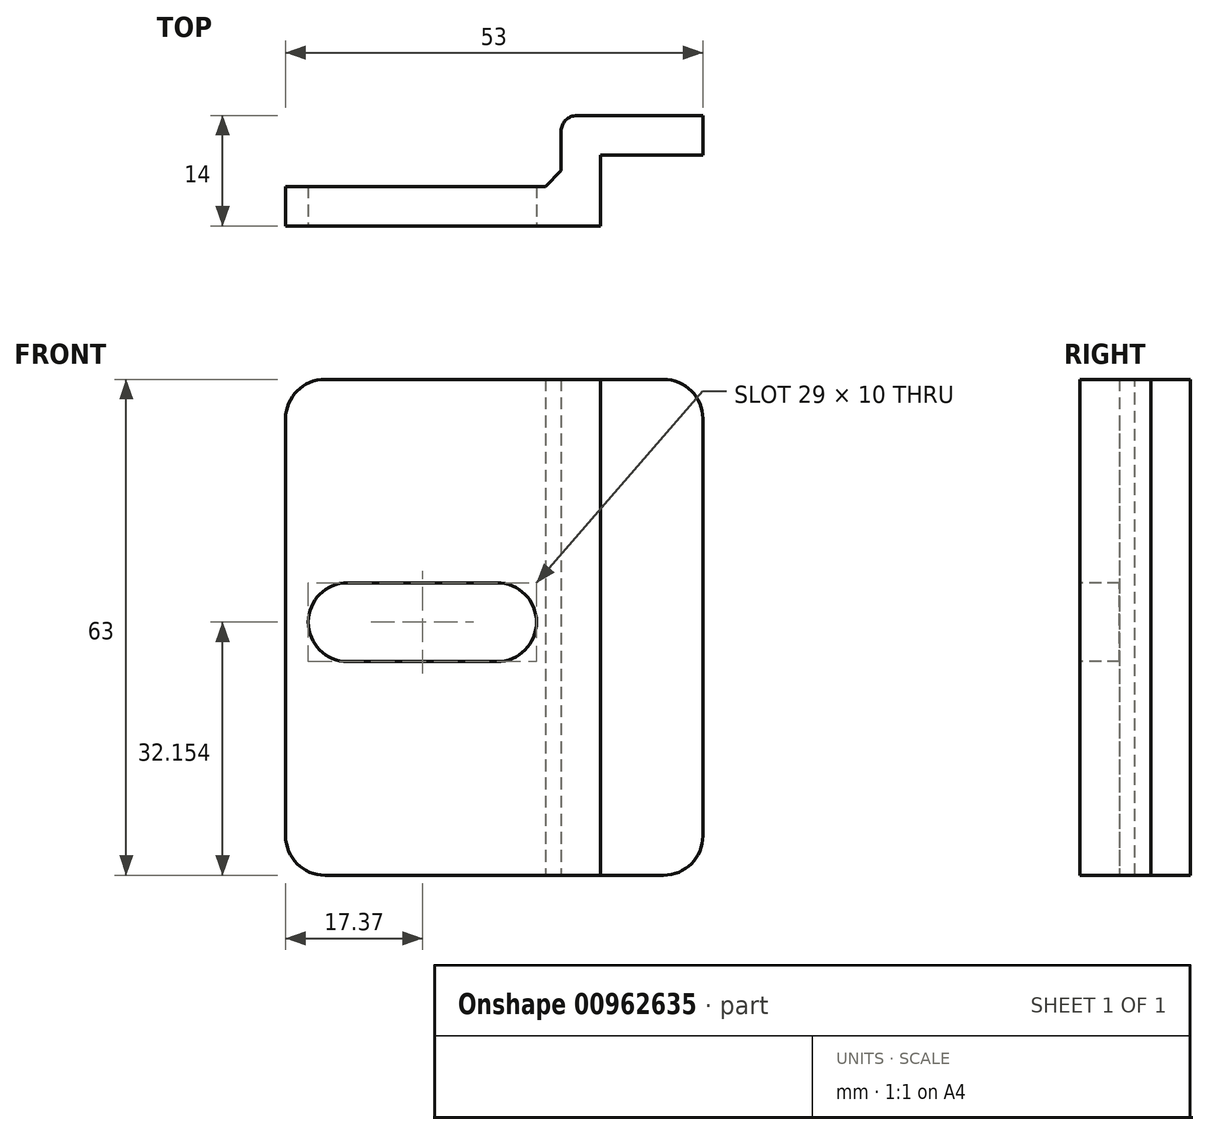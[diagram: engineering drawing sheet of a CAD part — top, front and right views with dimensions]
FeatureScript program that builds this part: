
annotation { "Feature Type Name" : "Feature", "Feature Type Description" : "" }
export const myFeature = defineFeature(function(context is Context, id is Id, definition is map)
    precondition{}
    {
        {
            var Q0;
            Q0=qCreatedBy(makeId("Top.planeOp"),FACE);
            var sketch = newSketch(context, id + "F0", { "sketchPlane" : qUnion([Q0])});
            skLineSegment(sketch, "E0.bottom", {"start": v(-6.28, 23.67) * mm, "end": v(11.72, 23.67) * mm});
            skLineSegment(sketch, "E0.top", {"start": v(-6.28, 18.67) * mm, "end": v(11.72, 18.67) * mm});
            skLineSegment(sketch, "E0.left", {"start": v(-6.28, 23.67) * mm, "end": v(-6.28, 18.67) * mm});
            skLineSegment(sketch, "E0.right", {"start": v(11.72, 23.67) * mm, "end": v(11.72, 18.67) * mm});
            skLineSegment(sketch, "E1.bottom", {"start": v(-6.28, 23.67) * mm, "end": v(-1.28, 23.67) * mm});
            skLineSegment(sketch, "E1.top", {"start": v(-6.28, 9.67) * mm, "end": v(-1.28, 9.67) * mm});
            skLineSegment(sketch, "E1.left", {"start": v(-6.28, 23.67) * mm, "end": v(-6.28, 9.67) * mm});
            skLineSegment(sketch, "E1.right", {"start": v(-1.28, 23.67) * mm, "end": v(-1.28, 9.67) * mm});
            skLineSegment(sketch, "E2.bottom", {"start": v(-6.28, 9.67) * mm, "end": v(-41.28, 9.67) * mm});
            skLineSegment(sketch, "E2.top", {"start": v(-6.28, 14.67) * mm, "end": v(-41.28, 14.67) * mm});
            skLineSegment(sketch, "E2.left", {"start": v(-6.28, 9.67) * mm, "end": v(-6.28, 14.67) * mm});
            skLineSegment(sketch, "E2.right", {"start": v(-41.28, 9.67) * mm, "end": v(-41.28, 14.67) * mm});
            skSolve(sketch);
        }
        {
            var Q0;
            {var subQ0=sQuery(id+"F0.wireOp",EDGE,"E2.bottom");Q0=makeQuery(id+"F0.imprint","IMPRINT",FACE,{"disambiguationData":[TD([[makeQuery(id+"F0.imprint","IMPRINT",EDGE,{"derivedFrom":subQ0}),-1.0]])]});}
            var Q1;
            {var subQ1=sQuery(id+"F0.wireOp",EDGE,"E1.top");Q1=makeQuery(id+"F0.imprint","IMPRINT",FACE,{"disambiguationData":[TD([[makeQuery(id+"F0.imprint","IMPRINT",EDGE,{"derivedFrom":subQ1}),1.0]])]});}
            var Q2;
            {var subQ3=sQuery(id+"F0.wireOp",EDGE,"E0.right");Q2=makeQuery(id+"F0.imprint","IMPRINT",FACE,{"disambiguationData":[TD([[makeQuery(id+"F0.imprint","IMPRINT",EDGE,{"derivedFrom":subQ3}),-1.0]])]});}
            var Q3;
            {var subQ3=sQuery(id+"F0.wireOp",EDGE,"E0.left");Q3=makeQuery(id+"F0.imprint","IMPRINT",FACE,{"disambiguationData":[TD([[makeQuery(id+"F0.imprint","IMPRINT",EDGE,{"derivedFrom":subQ3}),1.0]])]});}
            extrude(context, id + "F1", {"entities" : qUnion([Q0, Q1, Q2, Q3]), "depth" : 63 * mm, "offsetDistance" : 25 * mm});
        }
        {
            var Q0;
            Q0=makeQuery(id+"F1.opExtrude","CAP_EDGE",EDGE,{"disambiguationData":[OSD([sQuery(id+"F0.wireOp",EDGE,"E2.right")])],"isStart":false});
            var Q1;
            Q1=makeQuery(id+"F1.opExtrude","CAP_EDGE",EDGE,{"disambiguationData":[OSD([sQuery(id+"F0.wireOp",EDGE,"E0.right")])],"isStart":false});
            var Q2;
            Q2=makeQuery(id+"F1.opExtrude","CAP_EDGE",EDGE,{"disambiguationData":[OSD([sQuery(id+"F0.wireOp",EDGE,"E2.right")])],"isStart":true});
            var Q3;
            Q3=makeQuery(id+"F1.opExtrude","CAP_EDGE",EDGE,{"disambiguationData":[OSD([sQuery(id+"F0.wireOp",EDGE,"E0.right")])],"isStart":true});
            fillet(context, id + "F2", {"entities" : qUnion([Q0, Q1, Q2, Q3]), "radius" : 5 * mm, "tangentPropagation" : true, "allowEdgeOverflow" : false});
        }
        {
            var Q0;
            Q0=qCreatedBy(makeId("Front.planeOp"),FACE);
            var sketch = newSketch(context, id + "F3", { "sketchPlane" : qUnion([Q0])});
            skLineSegment(sketch, "E3.bottom", {"start": v(-14.4, 27.15) * mm, "end": v(-33.4, 27.15) * mm});
            skLineSegment(sketch, "E3.top", {"start": v(-14.4, 37.15) * mm, "end": v(-33.4, 37.15) * mm});
            skLineSegment(sketch, "E3.left", {"start": v(-14.4, 27.15) * mm, "end": v(-14.4, 37.15) * mm});
            skLineSegment(sketch, "E3.right", {"start": v(-33.4, 27.15) * mm, "end": v(-33.4, 37.15) * mm});
            skArc(sketch, "E4", {"start": v(-14.4, 27.15) * mm, "mid": v(-9.4, 32.15) * mm, "end": v(-14.4, 37.15) * mm});
            skArc(sketch, "E5", {"start": v(-33.4, 37.15) * mm, "mid": v(-38.4, 32.15) * mm, "end": v(-33.4, 27.15) * mm});
            skSolve(sketch);
        }
        {
            var Q0;
            Q0=makeQuery(id+"F3.imprint","IMPRINT",FACE,{"disambiguationData":[TD([[makeQuery(id+"F3.imprint","IMPRINT",EDGE,{"derivedFrom":sQuery(id+"F3.wireOp",EDGE,"E3.bottom")}),-1.0]])]});
            var Q1;
            Q1=makeQuery(id+"F3.imprint","IMPRINT",FACE,{"disambiguationData":[TD([[makeQuery(id+"F3.imprint","IMPRINT",EDGE,{"derivedFrom":sQuery(id+"F3.wireOp",EDGE,"E3.left")}),-1.0]])]});
            var Q2;
            Q2=makeQuery(id+"F3.imprint","IMPRINT",FACE,{"disambiguationData":[TD([[makeQuery(id+"F3.imprint","IMPRINT",EDGE,{"derivedFrom":sQuery(id+"F3.wireOp",EDGE,"E3.right")}),1.0]])]});
            extrude(context, id + "F4", {"entities" : qUnion([Q0, Q1, Q2]), "operationType" : NewBodyOperationType.REMOVE, "oppositeDirection" : true, "depth" : 25 * mm, "offsetDistance" : 25 * mm});
        }
        {
            var Q0;
            Q0=makeQuery(id+"F1.opExtrude","SWEPT_EDGE",EDGE,{"disambiguationData":[OSD([sQuery(id+"F0.wireOp",EDGE,"E1.left"),sQuery(id+"F0.wireOp",EDGE,"E2.top")])]});
            chamfer(context, id + "F5", {"entities" : qUnion([Q0]), "width" : 2 * mm, "tangentPropagation" : true});
        }
        {
            var Q0;
            Q0=makeQuery(id+"F1.opExtrude","SWEPT_EDGE",EDGE,{"disambiguationData":[OSD([sQuery(id+"F0.wireOp",EDGE,"E0.bottom"),sQuery(id+"F0.wireOp",EDGE,"E0.left")])]});
            fillet(context, id + "F6", {"entities" : qUnion([Q0]), "radius" : 2 * mm, "tangentPropagation" : true, "allowEdgeOverflow" : false});
        }
    });
